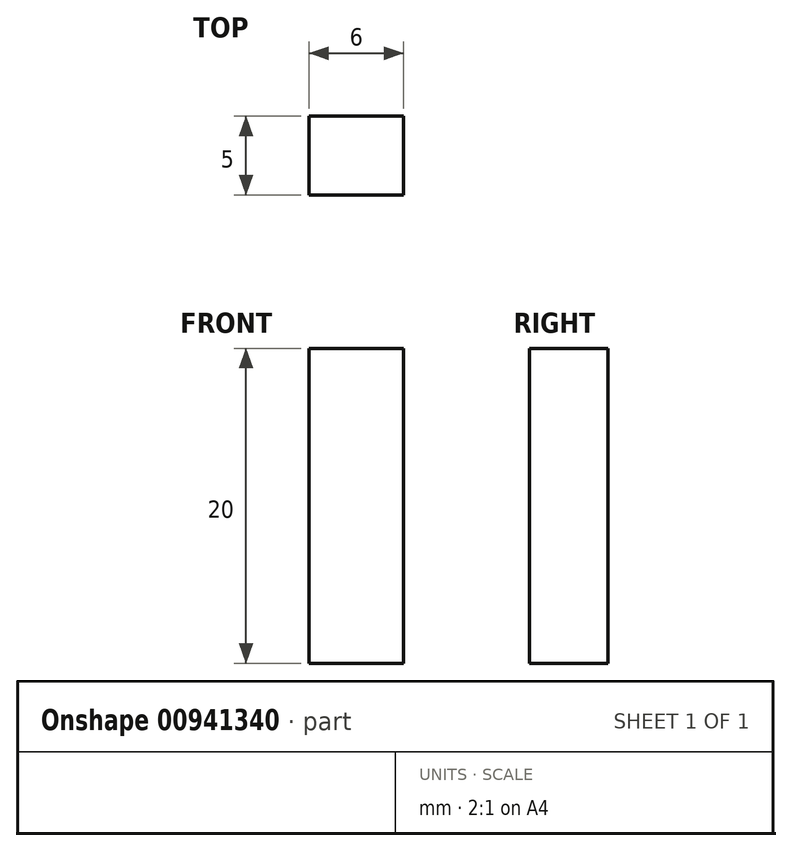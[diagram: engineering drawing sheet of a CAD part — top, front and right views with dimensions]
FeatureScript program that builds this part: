
annotation { "Feature Type Name" : "Feature", "Feature Type Description" : "" }
export const myFeature = defineFeature(function(context is Context, id is Id, definition is map)
    precondition{}
    {
        {
            var Q0;
            Q0=qCreatedBy(makeId("Front.planeOp"),FACE);
            var sketch = newSketch(context, id + "F0", { "sketchPlane" : qUnion([Q0])});
            skLineSegment(sketch, "E0", {"start": v(0, 0) * mm, "end": v(0, 10) * mm});
            skLineSegment(sketch, "E1", {"start": v(0, 0) * mm, "end": v(0, -10) * mm});
            skLineSegment(sketch, "E2", {"start": v(0, 10) * mm, "end": v(-3, 10) * mm});
            skLineSegment(sketch, "E3", {"start": v(0, 10) * mm, "end": v(3, 10) * mm});
            skLineSegment(sketch, "E4", {"start": v(-3, 10) * mm, "end": v(-3, -10) * mm});
            skLineSegment(sketch, "E5", {"start": v(3, 10) * mm, "end": v(3, -10) * mm});
            skLineSegment(sketch, "E6", {"start": v(3, -10) * mm, "end": v(-3, -10) * mm});
            skSolve(sketch);
        }
        {
            var Q0;
            Q0=makeQuery(id+"F0.imprint","IMPRINT",FACE,{"disambiguationData":[TD([[makeQuery(id+"F0.imprint","IMPRINT",EDGE,{"derivedFrom":sQuery(id+"F0.wireOp",EDGE,"E0")}),-1.0]])]});
            var Q1;
            Q1=makeQuery(id+"F0.imprint","IMPRINT",FACE,{"disambiguationData":[TD([[makeQuery(id+"F0.imprint","IMPRINT",EDGE,{"derivedFrom":sQuery(id+"F0.wireOp",EDGE,"E0")}),1.0]])]});
            extrude(context, id + "F1", {"entities" : qUnion([Q0, Q1]), "oppositeDirection" : true, "depth" : 5 * mm, "offsetDistance" : 25 * mm});
        }
    });
